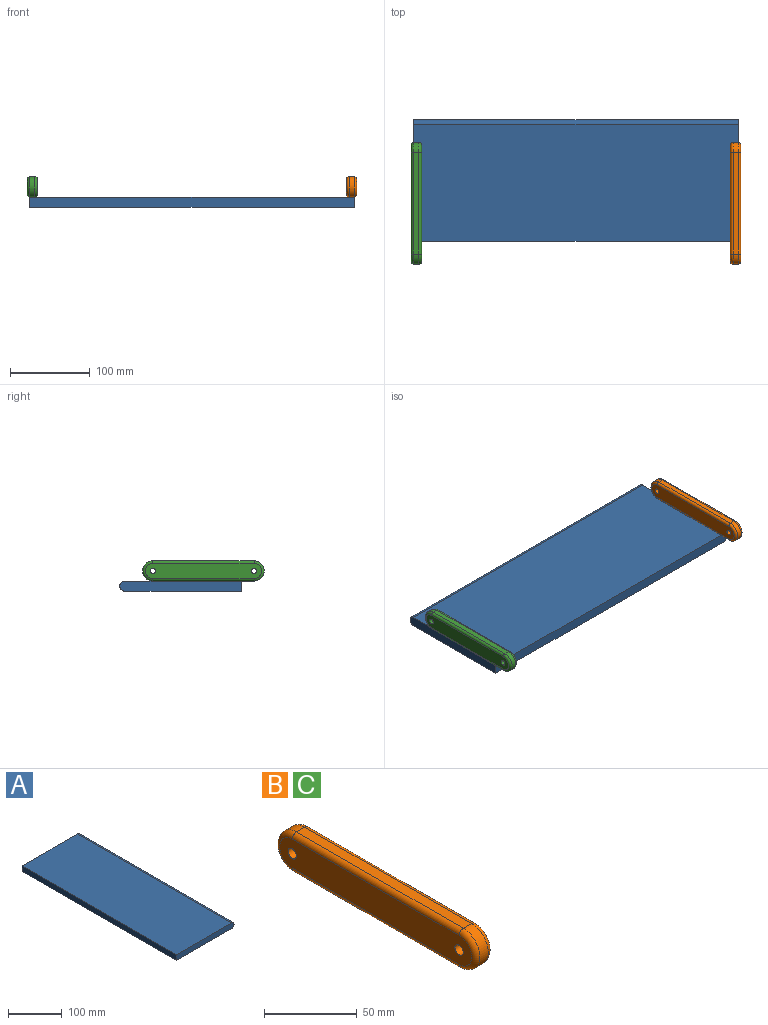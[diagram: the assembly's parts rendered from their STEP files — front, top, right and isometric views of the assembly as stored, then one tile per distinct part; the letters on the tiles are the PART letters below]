
ASSEMBLY  parts=3 mates=2
PART A: 6 faces, bbox 152.4x406.4x12.7 mm
  f0: plane 406.4x12.7mm, normal (-1,0,0), area 5161.3mm2, adj f1,f2,f3,f4
  f1: plane 152.4x12.7mm, normal (0,-1,0), area 1918.2mm2, adj f0,f3,f4,f5
  f2: plane 152.4x12.7mm, normal (0,1,0), area 1918.2mm2, adj f0,f3,f4,f5
  f3: plane 406.4x146.05mm, normal (0,0,1), area 59354.7mm2, adj f0,f1,f2,f5
  f4: plane 406.4x146.05mm, normal (0,0,-1), area 59354.7mm2, adj f0,f1,f2,f5
  f5: cylinder r=6.35mm len=406.4mm, axis (0,-1,0), area 8107.3mm2, adj f1,f2,f3,f4
PART B: 16 faces, bbox 12.7x154.5x27.5 mm
  f0: plane 127x6.35mm, normal (0,0,-1), area 806.5mm2, adj f4,f5,f11,f15
  f1: plane 127x6.35mm, normal (0,0,1), area 806.5mm2, adj f4,f5,f8,f12
  f2: plane 146.05x19.05mm, normal (1,0,0), area 2641mm2, adj f6,f7,f8,f9,f10,f11
  f3: plane 146.05x19.05mm, normal (-1,0,0), area 2641mm2, adj f6,f7,f12,f13,f14,f15
  f4: cylinder r=12.7mm len=25.4mm, axis (-1,0,0), area 253.4mm2, adj f0,f1,f9,f13
  f5: cylinder r=12.7mm len=25.4mm, axis (1,0,0), area 253.4mm2, adj f0,f1,f10,f14
  f6: cylinder r=3.17mm len=12.7mm, axis (1,0,0), area 253.4mm2, adj f2,f3
  f7: cylinder r=3.17mm len=12.7mm, axis (1,0,0), area 253.4mm2, adj f2,f3
  f8: cylinder r=3.17mm len=127mm, axis (0,1,0), area 633.4mm2, adj f1,f2,f9,f10
  f9: torus R=9.53mm, axis (1,0,0), area 180.9mm2, adj f2,f4,f8,f11
  f10: torus R=9.53mm, axis (1,0,0), area 180.9mm2, adj f2,f5,f8,f11
  f11: cylinder r=3.17mm len=127mm, axis (0,-1,0), area 633.4mm2, adj f0,f2,f9,f10
  f12: cylinder r=3.17mm len=127mm, axis (0,-1,0), area 633.4mm2, adj f1,f3,f13,f14
  f13: torus R=9.53mm, axis (1,0,0), area 180.9mm2, adj f3,f4,f12,f15
  f14: torus R=9.53mm, axis (1,0,0), area 180.9mm2, adj f3,f5,f12,f15
  f15: cylinder r=3.17mm len=127mm, axis (0,1,0), area 633.4mm2, adj f0,f3,f13,f14
PART C: same geometry as B
PLACE A rot(axis=(0,0,1),90deg) t=(355.95,-856.52,-799.79)mm
PLACE B t=(346.43,-885.1,-787.09)mm
PLACE C t=(-53.62,-885.1,-787.09)mm
MATE fastened A.f3 <-> C.f0  axis (0,0,1) through (-50.45,-783.5,-787.09)mm
MATE fastened B.f0 <-> A.f3  axis (0,0,-1) through (355.95,-783.5,-787.09)mm
